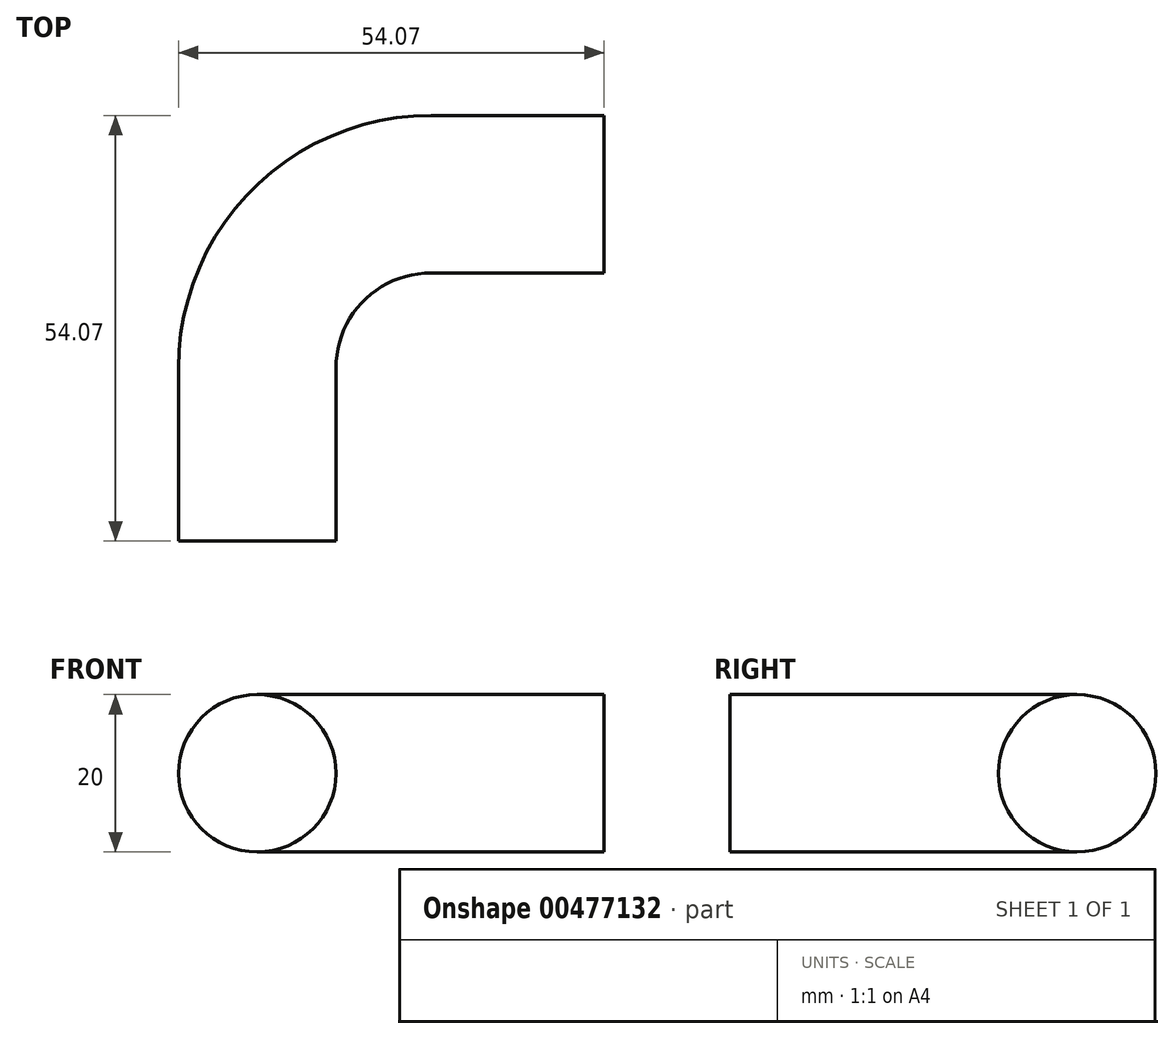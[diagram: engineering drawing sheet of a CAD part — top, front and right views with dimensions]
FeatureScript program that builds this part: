
annotation { "Feature Type Name" : "Feature", "Feature Type Description" : "" }
export const myFeature = defineFeature(function(context is Context, id is Id, definition is map)
    precondition{}
    {
        {
            var Q0;
            Q0=qCreatedBy(makeId("Front.planeOp"),FACE);
            var sketch = newSketch(context, id + "F0", { "sketchPlane" : qUnion([Q0])});
            skCircle(sketch, "E0", {"center": v(0, 0) * mm, "radius": 10 * mm});
            skSolve(sketch);
        }
        {
            var Q0;
            Q0=qCreatedBy(makeId("Top.planeOp"),FACE);
            var sketch = newSketch(context, id + "F1", { "sketchPlane" : qUnion([Q0])});
            skArc(sketch, "E1", {"start": v(0, 22) * mm, "mid": v(6.46, 37.6) * mm, "end": v(22.07, 44.07) * mm});
            skLineSegment(sketch, "E2", {"start": v(0, 0) * mm, "end": v(0, 22) * mm});
            skLineSegment(sketch, "E3", {"start": v(22.07, 44.07) * mm, "end": v(44.07, 44.07) * mm});
            skPoint(sketch, "E4.0", {"position": v(0, 0) * mm});
            skLineSegment(sketch, "E5.0", {"start": v(10, 0) * mm, "end": v(-10, 0) * mm, "construction": true});
            skSolve(sketch);
        }
        {
            var Q0;
            Q0 = qSketchRegion(id + "F0", true);
            var Q1;
            Q1 = qConstructionFilter(qBodyType(qCreatedBy(id + "F1" ,EDGE), BodyType.WIRE), ConstructionObject.NO);
            sweep(context, id + "F2", {"profiles" : qUnion([Q0]), "path" : qUnion([Q1])});
        }
    });
